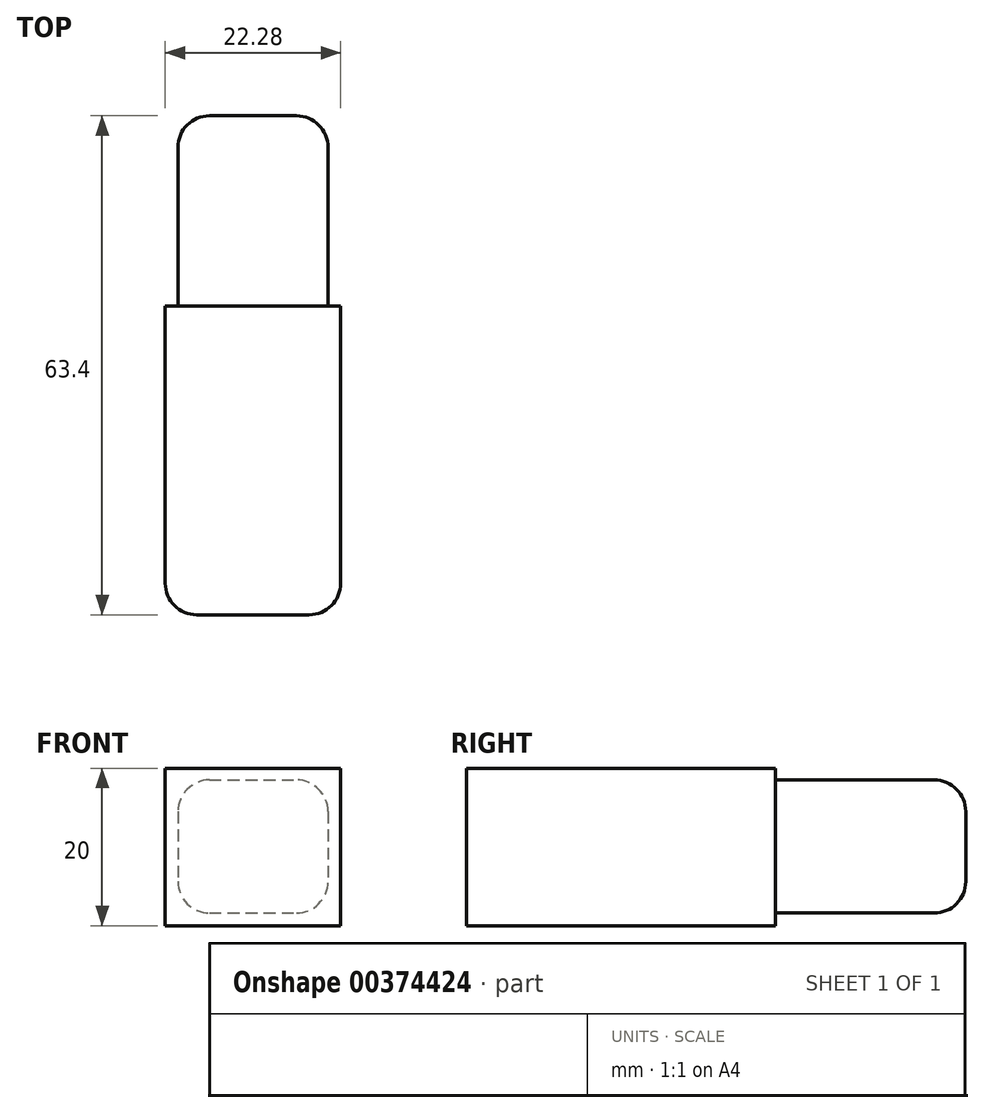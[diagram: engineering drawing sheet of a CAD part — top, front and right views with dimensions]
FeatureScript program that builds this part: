
annotation { "Feature Type Name" : "Feature", "Feature Type Description" : "" }
export const myFeature = defineFeature(function(context is Context, id is Id, definition is map)
    precondition{}
    {
        {
            var Q0;
            Q0=qCreatedBy(makeId("Top.planeOp"),FACE);
            var sketch = newSketch(context, id + "F0", { "sketchPlane" : qUnion([Q0])});
            skLineSegment(sketch, "E0.bottom", {"start": v(11.14, 19.6) * mm, "end": v(-11.14, 19.6) * mm});
            skLineSegment(sketch, "E0.top", {"start": v(11.14, -19.6) * mm, "end": v(-11.14, -19.6) * mm});
            skLineSegment(sketch, "E0.left", {"start": v(11.14, 19.6) * mm, "end": v(11.14, -19.6) * mm});
            skLineSegment(sketch, "E0.right", {"start": v(-11.14, 19.6) * mm, "end": v(-11.14, -19.6) * mm});
            skPoint(sketch, "E0.middle", {"position": v(0, 0) * mm});
            skSolve(sketch);
        }
        {
            var Q0;
            Q0=qSketchRegion(id+"F0",true);
            extrude(context, id + "F1", {"entities" : qUnion([Q0]), "depth" : 20 * mm});
        }
        {
            var Q0;
            Q0=makeQuery(id+"F1.opExtrude","SWEPT_EDGE",EDGE,{"disambiguationData":[OSD([sQuery(id+"F0.wireOp",EDGE,"E0.top"),sQuery(id+"F0.wireOp",EDGE,"E0.right")])]});
            var Q1;
            Q1=makeQuery(id+"F1.opExtrude","SWEPT_EDGE",EDGE,{"disambiguationData":[OSD([sQuery(id+"F0.wireOp",EDGE,"E0.top"),sQuery(id+"F0.wireOp",EDGE,"E0.left")])]});
            fillet(context, id + "F2", {"entities" : qUnion([Q0, Q1]), "radius" : 4 * mm, "tangentPropagation" : true, "allowEdgeOverflow" : false});
        }
        {
            var Q0;
            Q0=makeQuery(id+"F1.opExtrude","SWEPT_FACE",FACE,{"disambiguationData":[OSD([sQuery(id+"F0.wireOp",EDGE,"E0.bottom")])]});
            var sketch = newSketch(context, id + "F3", { "sketchPlane" : qUnion([Q0])});
            skLineSegment(sketch, "E1.bottom", {"start": v(9.53, 18.52) * mm, "end": v(-9.53, 18.52) * mm});
            skLineSegment(sketch, "E1.top", {"start": v(9.53, 1.62) * mm, "end": v(-9.53, 1.62) * mm});
            skLineSegment(sketch, "E1.left", {"start": v(9.53, 18.52) * mm, "end": v(9.53, 1.62) * mm});
            skLineSegment(sketch, "E1.right", {"start": v(-9.53, 18.52) * mm, "end": v(-9.53, 1.62) * mm});
            skPoint(sketch, "E1.middle", {"position": v(0, 10.07) * mm});
            skSolve(sketch);
        }
        {
            var Q0;
            Q0=makeQuery(id+"F3.imprint","IMPRINT",FACE,{"disambiguationData":[TD([[makeQuery(id+"F3.imprint","IMPRINT",EDGE,{"derivedFrom":sQuery(id+"F3.wireOp",EDGE,"E1.bottom")}),1.0]])]});
            extrude(context, id + "F4", {"entities" : qUnion([Q0]), "operationType" : NewBodyOperationType.ADD, "depth" : 24.2 * mm});
        }
        {
            var Q0;
            Q0=makeQuery(id+"F4.opExtrude","SWEPT_EDGE",EDGE,{"disambiguationData":[OSD([sQuery(id+"F3.wireOp",EDGE,"E1.top"),sQuery(id+"F3.wireOp",EDGE,"E1.left")])]});
            var Q1;
            Q1=makeQuery(id+"F4.opExtrude","SWEPT_EDGE",EDGE,{"disambiguationData":[OSD([sQuery(id+"F3.wireOp",EDGE,"E1.top"),sQuery(id+"F3.wireOp",EDGE,"E1.right")])]});
            var Q2;
            Q2=makeQuery(id+"F4.opExtrude","SWEPT_EDGE",EDGE,{"disambiguationData":[OSD([sQuery(id+"F3.wireOp",EDGE,"E1.bottom"),sQuery(id+"F3.wireOp",EDGE,"E1.left")])]});
            var Q3;
            Q3=makeQuery(id+"F4.opExtrude","SWEPT_EDGE",EDGE,{"disambiguationData":[OSD([sQuery(id+"F3.wireOp",EDGE,"E1.bottom"),sQuery(id+"F3.wireOp",EDGE,"E1.right")])]});
            fillet(context, id + "F5", {"entities" : qUnion([Q0, Q1, Q2, Q3]), "radius" : 4 * mm, "tangentPropagation" : true, "allowEdgeOverflow" : false});
        }
        {
            var Q0;
            Q0=makeQuery(id+"F4.opExtrude","CAP_EDGE",EDGE,{"disambiguationData":[OSD([sQuery(id+"F3.wireOp",EDGE,"E1.right")])],"isStart":false});
            var Q1;
            Q1=makeQuery(id+"F4.opExtrude","CAP_EDGE",EDGE,{"disambiguationData":[OSD([sQuery(id+"F3.wireOp",EDGE,"E1.bottom")])],"isStart":false});
            var Q2;
            Q2=makeQuery(id+"F4.opExtrude","CAP_EDGE",EDGE,{"disambiguationData":[OSD([sQuery(id+"F3.wireOp",EDGE,"E1.left")])],"isStart":false});
            var Q3;
            Q3=makeQuery(id+"F4.opExtrude","CAP_EDGE",EDGE,{"disambiguationData":[OSD([sQuery(id+"F3.wireOp",EDGE,"E1.top")])],"isStart":false});
            fillet(context, id + "F6", {"entities" : qUnion([Q0, Q1, Q2, Q3]), "radius" : 4 * mm, "tangentPropagation" : true, "allowEdgeOverflow" : false});
        }
    });
